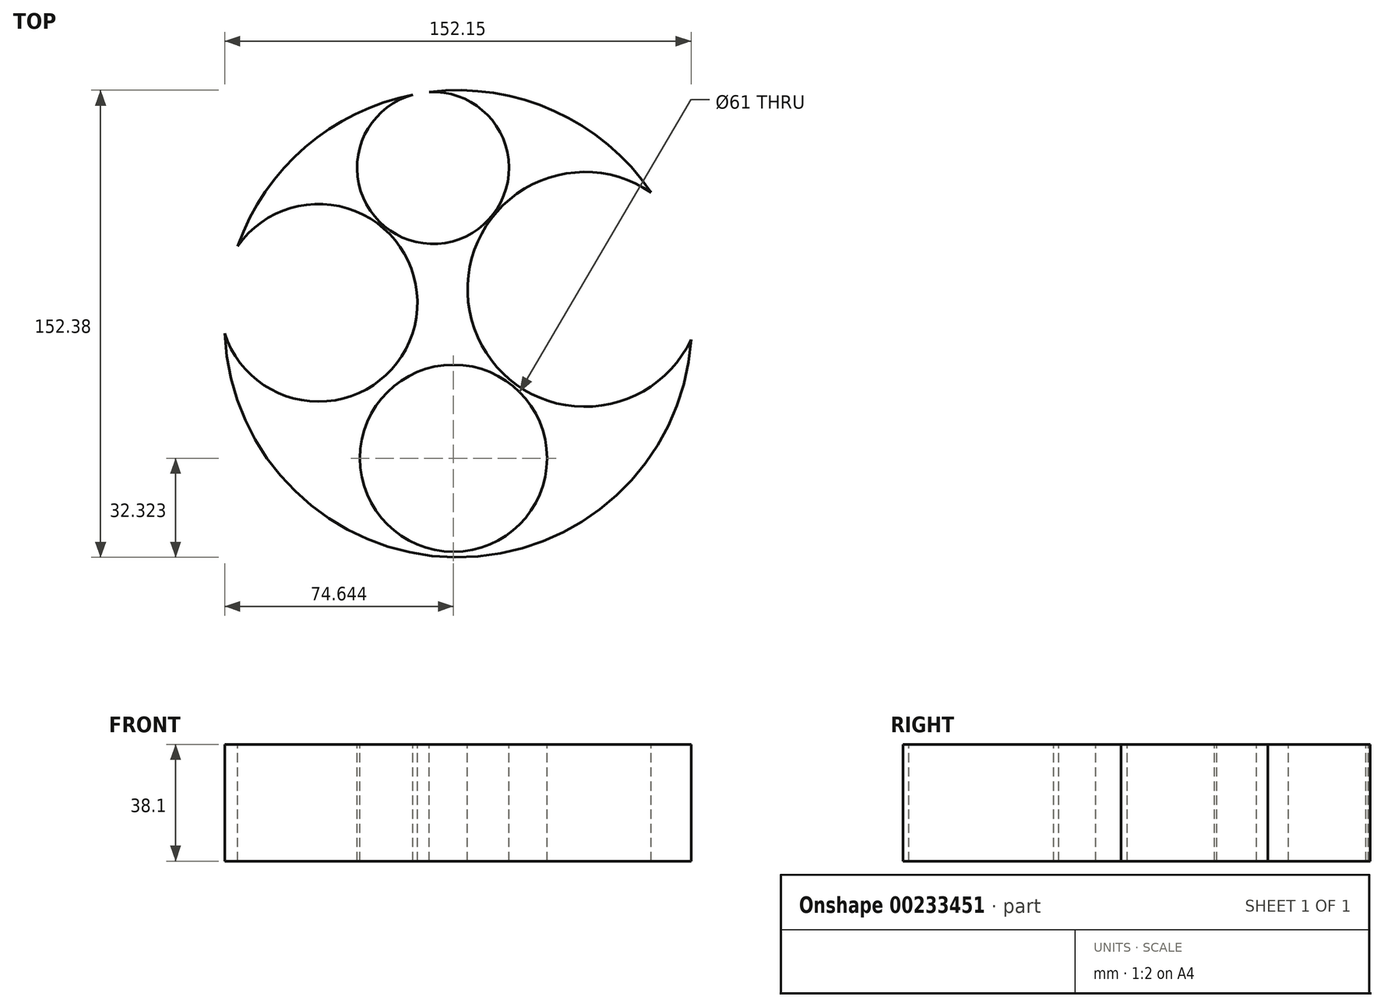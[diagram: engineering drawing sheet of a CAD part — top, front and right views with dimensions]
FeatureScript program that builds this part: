
annotation { "Feature Type Name" : "Feature", "Feature Type Description" : "" }
export const myFeature = defineFeature(function(context is Context, id is Id, definition is map)
    precondition{}
    {
        {
            var Q0;
            Q0=qCreatedBy(makeId("Top.planeOp"),FACE);
            var sketch = newSketch(context, id + "F0", { "sketchPlane" : qUnion([Q0])});
            skCircle(sketch, "E0", {"center": v(0, 0) * mm, "radius": 76.2 * mm});
            skSolve(sketch);
        }
        {
            var Q0;
            Q0=makeQuery(id+"F0.imprint","IMPRINT",FACE,{"disambiguationData":[TD([[makeQuery(id+"F0.imprint","IMPRINT",EDGE,{"derivedFrom":sQuery(id+"F0.wireOp",EDGE,"E0")}),1.0]])]});
            extrude(context, id + "F1", {"entities" : qUnion([Q0]), "depth" : 12.7 * mm});
        }
        {
            var Q0;
            Q0=makeQuery(id+"F1.opExtrude","CAP_FACE",FACE,{"disambiguationData":[OSD([sQuery(id+"F0.wireOp",EDGE,"E0")])],"isStart":false});
            var sketch = newSketch(context, id + "F2", { "sketchPlane" : qUnion([Q0])});
            skCircle(sketch, "E1", {"center": v(41.39, 11.22) * mm, "radius": 38.3 * mm});
            skCircle(sketch, "E2", {"center": v(-8.16, 50.86) * mm, "radius": 24.78 * mm});
            skCircle(sketch, "E3", {"center": v(-45.47, 6.85) * mm, "radius": 32.23 * mm});
            skCircle(sketch, "E4", {"center": v(0, -43.87) * mm, "radius": 1.49 * mm});
            skCircle(sketch, "E5", {"center": v(-1.49, -43.87) * mm, "radius": 30.5 * mm});
            skSolve(sketch);
        }
        {
            var Q0;
            Q0=makeQuery(id+"F2.imprint","IMPRINT",FACE,{"disambiguationData":[TD([[makeQuery(id+"F2.imprint","IMPRINT",EDGE,{"derivedFrom":sQuery(id+"F2.wireOp",EDGE,"E4")}),-1.0]])]});
            var Q1;
            {var subQ0=sQuery(id+"F2.wireOp",EDGE,"E1");var subQ1=makeQuery(id+"F1.opExtrude","CAP_EDGE",EDGE,{"disambiguationData":[OSD([sQuery(id+"F0.wireOp",EDGE,"E0")])],"isStart":false});var subQ2=makeQuery(id+"F2.imprint","INTERSECT",VERTEX,{"disambiguationData":[OD(0.0)],"derivedFrom":[subQ1,subQ0]});Q1=makeQuery(id+"F2.imprint","IMPRINT",FACE,{"disambiguationData":[TD([[makeQuery(id+"F2.imprint","IMPRINT",EDGE,{"disambiguationData":[TD([[subQ2,-1.0]])],"derivedFrom":subQ0}),1.0]])]});}
            var Q2;
            {var subQ0=sQuery(id+"F2.wireOp",EDGE,"E2");var subQ1=makeQuery(id+"F1.opExtrude","CAP_EDGE",EDGE,{"disambiguationData":[OSD([sQuery(id+"F0.wireOp",EDGE,"E0")])],"isStart":false});var subQ2=makeQuery(id+"F2.imprint","INTERSECT",VERTEX,{"disambiguationData":[OD(0.0)],"derivedFrom":[subQ1,subQ0]});Q2=makeQuery(id+"F2.imprint","IMPRINT",FACE,{"disambiguationData":[TD([[makeQuery(id+"F2.imprint","IMPRINT",EDGE,{"disambiguationData":[TD([[subQ2,1.0]])],"derivedFrom":subQ0}),1.0]])]});}
            var Q3;
            {var subQ0=sQuery(id+"F2.wireOp",EDGE,"E3");var subQ1=makeQuery(id+"F1.opExtrude","CAP_EDGE",EDGE,{"disambiguationData":[OSD([sQuery(id+"F0.wireOp",EDGE,"E0")])],"isStart":false});var subQ2=makeQuery(id+"F2.imprint","INTERSECT",VERTEX,{"disambiguationData":[OD(0.0)],"derivedFrom":[subQ1,subQ0]});Q3=makeQuery(id+"F2.imprint","IMPRINT",FACE,{"disambiguationData":[TD([[makeQuery(id+"F2.imprint","IMPRINT",EDGE,{"disambiguationData":[TD([[subQ2,1.0]])],"derivedFrom":subQ0}),1.0]])]});}
            var Q4;
            {var subQ0=sQuery(id+"F2.wireOp",EDGE,"E2");var subQ1=makeQuery(id+"F1.opExtrude","CAP_EDGE",EDGE,{"disambiguationData":[OSD([sQuery(id+"F0.wireOp",EDGE,"E0")])],"isStart":false});var subQ2=makeQuery(id+"F2.imprint","INTERSECT",VERTEX,{"disambiguationData":[OD(0.0)],"derivedFrom":[subQ1,subQ0]});Q4=makeQuery(id+"F2.imprint","IMPRINT",FACE,{"disambiguationData":[TD([[makeQuery(id+"F2.imprint","IMPRINT",EDGE,{"disambiguationData":[TD([[subQ2,-1.0]])],"derivedFrom":subQ0}),1.0]])]});}
            var Q5;
            {var subQ0=sQuery(id+"F2.wireOp",EDGE,"E3");var subQ1=makeQuery(id+"F1.opExtrude","CAP_EDGE",EDGE,{"disambiguationData":[OSD([sQuery(id+"F0.wireOp",EDGE,"E0")])],"isStart":false});var subQ2=makeQuery(id+"F2.imprint","INTERSECT",VERTEX,{"disambiguationData":[OD(0.0)],"derivedFrom":[subQ1,subQ0]});Q5=makeQuery(id+"F2.imprint","IMPRINT",FACE,{"disambiguationData":[TD([[makeQuery(id+"F2.imprint","IMPRINT",EDGE,{"disambiguationData":[TD([[subQ2,-1.0]])],"derivedFrom":subQ0}),1.0]])]});}
            var Q6;
            {var subQ0=sQuery(id+"F2.wireOp",EDGE,"E1");var subQ1=makeQuery(id+"F1.opExtrude","CAP_EDGE",EDGE,{"disambiguationData":[OSD([sQuery(id+"F0.wireOp",EDGE,"E0")])],"isStart":false});var subQ2=makeQuery(id+"F2.imprint","INTERSECT",VERTEX,{"disambiguationData":[OD(0.0)],"derivedFrom":[subQ1,subQ0]});Q6=makeQuery(id+"F2.imprint","IMPRINT",FACE,{"disambiguationData":[TD([[makeQuery(id+"F2.imprint","IMPRINT",EDGE,{"disambiguationData":[TD([[subQ2,1.0]])],"derivedFrom":subQ0}),1.0]])]});}
            extrude(context, id + "F3", {"entities" : qUnion([Q0, Q1, Q2, Q3, Q4, Q5, Q6]), "operationType" : NewBodyOperationType.REMOVE, "endBound" : BoundingType.THROUGH_ALL, "oppositeDirection" : true, "depth" : 25.4 * mm});
        }
        {
            var Q0;
            {var subQ0=sQuery(id+"F0.wireOp",EDGE,"E0");Q0=makeQuery(id+"F3.boolean.opBoolean","SPLIT",FACE,{"disambiguationData":[TD([makeQuery(id+"F1.opExtrude","SWEPT_FACE",FACE,{"disambiguationData":[OSD([subQ0])]})])],"derivedFrom":makeQuery(id+"F1.opExtrude","CAP_FACE",FACE,{"disambiguationData":[OSD([subQ0])],"isStart":false})});}
            extrude(context, id + "F4", {"entities" : qUnion([Q0]), "operationType" : NewBodyOperationType.ADD, "depth" : 25.4 * mm});
        }
        {
            var Q0;
            Q0=makeQuery(id+"F4.opExtrude","CAP_FACE",FACE,{"disambiguationData":[OSD([sQuery(id+"F0.wireOp",EDGE,"E0")])],"isStart":false});
            extrude(context, id + "F5", {"entities" : qUnion([Q0]), "operationType" : NewBodyOperationType.REMOVE, "oppositeDirection" : true, "depth" : 25.4 * mm});
        }
        {
            var Q0;
            Q0=makeQuery(id+"F3.boolean.opBoolean","SPLIT",FACE,{"disambiguationData":[TD([makeQuery(id+"F3.opExtrude","SWEPT_FACE",FACE,{"disambiguationData":[OSD([sQuery(id+"F2.wireOp",EDGE,"E4")])]})])],"derivedFrom":makeQuery(id+"F1.opExtrude","CAP_FACE",FACE,{"disambiguationData":[OSD([sQuery(id+"F0.wireOp",EDGE,"E0")])],"isStart":false})});
            extrude(context, id + "F6", {"entities" : qUnion([Q0]), "operationType" : NewBodyOperationType.REMOVE, "oppositeDirection" : true, "depth" : 25.4 * mm});
        }
        {
            var Q0;
            Q0=makeQuery(id+"F5.boolean.opBoolean","COPY",FACE,{"derivedFrom":makeQuery(id+"F5.opExtrude","CAP_FACE",FACE,{"disambiguationData":[OSD([sQuery(id+"F0.wireOp",EDGE,"E0")])],"isStart":false})});
            extrude(context, id + "F7", {"entities" : qUnion([Q0]), "operationType" : NewBodyOperationType.ADD, "depth" : 25.4 * mm});
        }
    });
